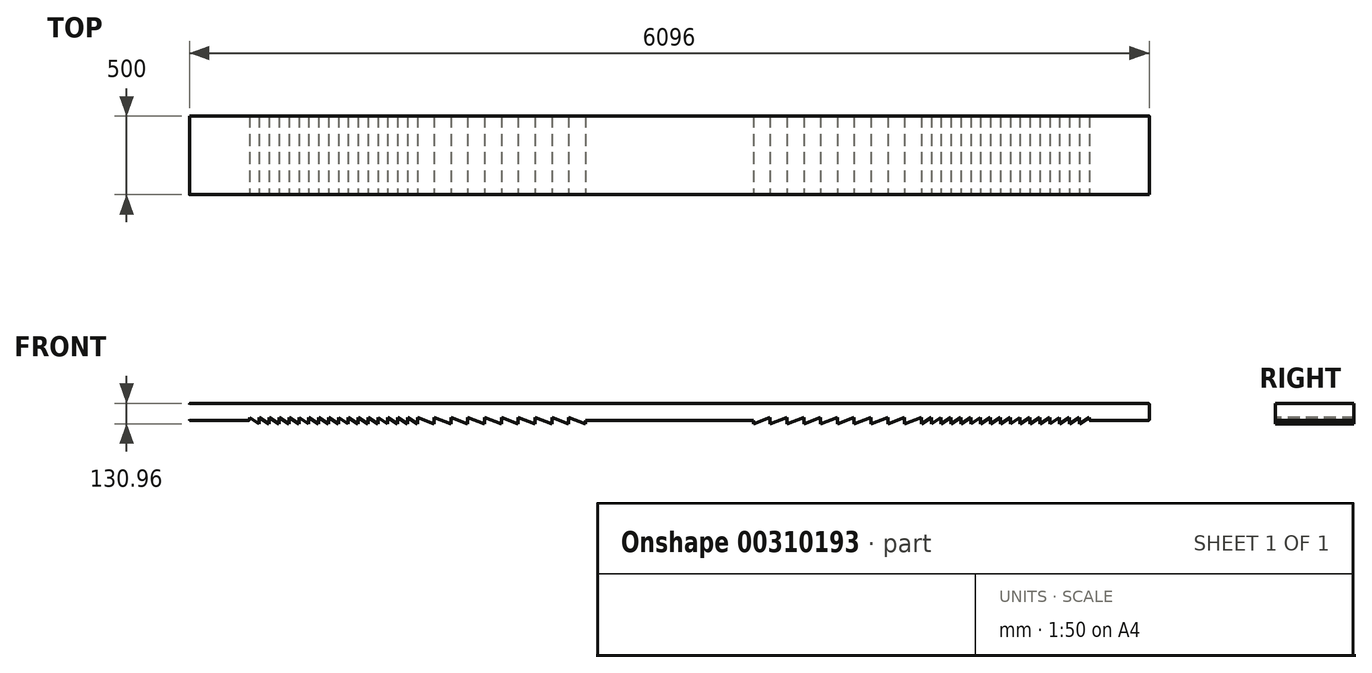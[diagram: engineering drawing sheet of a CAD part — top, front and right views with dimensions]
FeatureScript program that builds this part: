
annotation { "Feature Type Name" : "Feature", "Feature Type Description" : "" }
export const myFeature = defineFeature(function(context is Context, id is Id, definition is map)
    precondition{}
    {
        {
            var Q0;
            Q0=qCreatedBy(makeId("Front.planeOp"),FACE);
            var sketch = newSketch(context, id + "F0", { "sketchPlane" : qUnion([Q0])});
            skLineSegment(sketch, "E0", {"start": v(-3048, 59.13) * mm, "end": v(-3048, -37.9) * mm});
            skArc(sketch, "E1", {"start": v(-3048, -37.9) * mm, "mid": v(-3046.14, -42.4) * mm, "end": v(-3041.65, -44.25) * mm});
            skLineSegment(sketch, "E2", {"start": v(-3041.65, -44.25) * mm, "end": v(-2673.35, -44.25) * mm});
            skArc(sketch, "E3", {"start": v(-2673.35, -44.25) * mm, "mid": v(-2668.86, -42.4) * mm, "end": v(-2667, -37.9) * mm});
            skLineSegment(sketch, "E4", {"start": v(-2667, -37.9) * mm, "end": v(-2667, -23.42) * mm});
            skLineSegment(sketch, "E5", {"start": v(-2667, -23.42) * mm, "end": v(-2604.26, -65.45) * mm});
            skLineSegment(sketch, "E6", {"start": v(-2604.26, -65.45) * mm, "end": v(-2604.26, -23.41) * mm});
            skLineSegment(sketch, "E7", {"start": v(-2604.26, -23.41) * mm, "end": v(-2541.5, -65.45) * mm});
            skLineSegment(sketch, "E8", {"start": v(-2541.5, -65.45) * mm, "end": v(-2541.5, -23.41) * mm});
            skLineSegment(sketch, "E9", {"start": v(-2541.5, -23.41) * mm, "end": v(-2478.76, -65.45) * mm});
            skLineSegment(sketch, "E10", {"start": v(-2478.76, -65.45) * mm, "end": v(-2478.76, -23.41) * mm});
            skLineSegment(sketch, "E11", {"start": v(-2478.76, -23.41) * mm, "end": v(-2416, -65.45) * mm});
            skLineSegment(sketch, "E12", {"start": v(-2416, -65.45) * mm, "end": v(-2416, -23.41) * mm});
            skLineSegment(sketch, "E13", {"start": v(-2416, -23.41) * mm, "end": v(-2353.25, -65.45) * mm});
            skLineSegment(sketch, "E14", {"start": v(-2353.25, -65.45) * mm, "end": v(-2353.25, -23.41) * mm});
            skLineSegment(sketch, "E15", {"start": v(-2353.25, -23.41) * mm, "end": v(-2290.5, -65.45) * mm});
            skLineSegment(sketch, "E16", {"start": v(-2290.5, -65.45) * mm, "end": v(-2290.5, -23.41) * mm});
            skLineSegment(sketch, "E17", {"start": v(-2290.5, -23.41) * mm, "end": v(-2227.74, -65.45) * mm});
            skLineSegment(sketch, "E18", {"start": v(-2227.74, -65.45) * mm, "end": v(-2227.74, -23.41) * mm});
            skLineSegment(sketch, "E19", {"start": v(-2227.74, -23.41) * mm, "end": v(-2165, -65.45) * mm});
            skLineSegment(sketch, "E20", {"start": v(-2165, -65.45) * mm, "end": v(-2165, -23.41) * mm});
            skLineSegment(sketch, "E21", {"start": v(-2165, -23.41) * mm, "end": v(-2102.24, -65.45) * mm});
            skLineSegment(sketch, "E22", {"start": v(-2102.24, -65.45) * mm, "end": v(-2102.24, -23.41) * mm});
            skLineSegment(sketch, "E23", {"start": v(-2102.24, -23.41) * mm, "end": v(-2039.49, -65.45) * mm});
            skLineSegment(sketch, "E24", {"start": v(-2039.49, -65.45) * mm, "end": v(-2039.49, -23.41) * mm});
            skLineSegment(sketch, "E25", {"start": v(-2039.49, -23.41) * mm, "end": v(-1976.73, -65.45) * mm});
            skLineSegment(sketch, "E26", {"start": v(-1976.73, -65.45) * mm, "end": v(-1976.73, -23.41) * mm});
            skLineSegment(sketch, "E27", {"start": v(-1976.73, -23.41) * mm, "end": v(-1913.98, -65.45) * mm});
            skLineSegment(sketch, "E28", {"start": v(-1913.98, -65.45) * mm, "end": v(-1913.98, -23.41) * mm});
            skLineSegment(sketch, "E29", {"start": v(-1913.98, -23.41) * mm, "end": v(-1851.23, -65.45) * mm});
            skLineSegment(sketch, "E30", {"start": v(-1851.23, -65.45) * mm, "end": v(-1851.23, -23.41) * mm});
            skLineSegment(sketch, "E31", {"start": v(-1851.23, -23.41) * mm, "end": v(-1788.47, -65.45) * mm});
            skLineSegment(sketch, "E32", {"start": v(-1788.47, -65.45) * mm, "end": v(-1788.47, -23.41) * mm});
            skLineSegment(sketch, "E33", {"start": v(-1788.47, -23.41) * mm, "end": v(-1725.72, -65.45) * mm});
            skLineSegment(sketch, "E34", {"start": v(-1725.72, -65.45) * mm, "end": v(-1725.72, -23.41) * mm});
            skLineSegment(sketch, "E35", {"start": v(-1725.72, -23.41) * mm, "end": v(-1662.97, -65.45) * mm});
            skLineSegment(sketch, "E36", {"start": v(-1662.97, -65.45) * mm, "end": v(-1662.97, -23.41) * mm});
            skLineSegment(sketch, "E37", {"start": v(-1662.97, -23.41) * mm, "end": v(-1600.21, -65.45) * mm});
            skLineSegment(sketch, "E38", {"start": v(-1600.21, -65.45) * mm, "end": v(-1600.21, -23.42) * mm});
            skLineSegment(sketch, "E39", {"start": v(-1600.21, -23.42) * mm, "end": v(-1493.53, -65.48) * mm});
            skLineSegment(sketch, "E40", {"start": v(-1493.53, -65.48) * mm, "end": v(-1493.53, -23.42) * mm});
            skLineSegment(sketch, "E41", {"start": v(-1493.53, -23.42) * mm, "end": v(-1386.85, -65.48) * mm});
            skLineSegment(sketch, "E42", {"start": v(-1386.85, -65.48) * mm, "end": v(-1386.85, -23.42) * mm});
            skLineSegment(sketch, "E43", {"start": v(-1386.85, -23.42) * mm, "end": v(-1280.17, -65.48) * mm});
            skLineSegment(sketch, "E44", {"start": v(-1280.17, -65.48) * mm, "end": v(-1280.17, -23.42) * mm});
            skLineSegment(sketch, "E45", {"start": v(-1280.17, -23.42) * mm, "end": v(-1173.5, -65.48) * mm});
            skLineSegment(sketch, "E46", {"start": v(-1173.5, -65.48) * mm, "end": v(-1173.5, -23.42) * mm});
            skLineSegment(sketch, "E47", {"start": v(-1173.5, -23.42) * mm, "end": v(-1066.81, -65.48) * mm});
            skLineSegment(sketch, "E48", {"start": v(-1066.81, -65.48) * mm, "end": v(-1066.81, -23.42) * mm});
            skLineSegment(sketch, "E49", {"start": v(-1066.81, -23.42) * mm, "end": v(-960.13, -65.48) * mm});
            skLineSegment(sketch, "E50", {"start": v(-960.13, -65.48) * mm, "end": v(-960.13, -23.42) * mm});
            skLineSegment(sketch, "E51", {"start": v(-960.13, -23.42) * mm, "end": v(-853.45, -65.48) * mm});
            skLineSegment(sketch, "E52", {"start": v(-853.45, -65.48) * mm, "end": v(-853.45, -23.42) * mm});
            skLineSegment(sketch, "E53", {"start": v(-853.45, -23.42) * mm, "end": v(-746.77, -65.48) * mm});
            skLineSegment(sketch, "E54", {"start": v(-746.77, -65.48) * mm, "end": v(-746.77, -23.42) * mm});
            skLineSegment(sketch, "E55", {"start": v(-746.77, -23.42) * mm, "end": v(-640.1, -65.48) * mm});
            skLineSegment(sketch, "E56", {"start": v(-640.1, -65.48) * mm, "end": v(-640.1, -23.42) * mm});
            skLineSegment(sketch, "E57", {"start": v(-640.1, -23.42) * mm, "end": v(-533.41, -65.48) * mm});
            skLineSegment(sketch, "E58", {"start": v(-533.41, -44.25) * mm, "end": v(-533.41, -65.48) * mm});
            skLineSegment(sketch, "E59", {"start": v(-533.41, -44.25) * mm, "end": v(533.41, -44.25) * mm});
            skLineSegment(sketch, "E60", {"start": v(533.41, -44.25) * mm, "end": v(533.41, -65.48) * mm});
            skLineSegment(sketch, "E61", {"start": v(533.41, -65.48) * mm, "end": v(640.1, -23.42) * mm});
            skLineSegment(sketch, "E62", {"start": v(640.1, -23.42) * mm, "end": v(640.1, -65.48) * mm});
            skLineSegment(sketch, "E63", {"start": v(640.1, -65.48) * mm, "end": v(746.77, -23.42) * mm});
            skLineSegment(sketch, "E64", {"start": v(746.77, -23.42) * mm, "end": v(746.77, -65.48) * mm});
            skLineSegment(sketch, "E65", {"start": v(746.77, -65.48) * mm, "end": v(853.45, -23.42) * mm});
            skLineSegment(sketch, "E66", {"start": v(853.45, -23.42) * mm, "end": v(853.45, -65.48) * mm});
            skLineSegment(sketch, "E67", {"start": v(853.45, -65.48) * mm, "end": v(960.13, -23.42) * mm});
            skLineSegment(sketch, "E68", {"start": v(960.13, -23.42) * mm, "end": v(960.13, -65.48) * mm});
            skLineSegment(sketch, "E69", {"start": v(960.13, -65.48) * mm, "end": v(1066.81, -23.42) * mm});
            skLineSegment(sketch, "E70", {"start": v(1066.81, -23.42) * mm, "end": v(1066.81, -65.48) * mm});
            skLineSegment(sketch, "E71", {"start": v(1066.81, -65.48) * mm, "end": v(1173.5, -23.42) * mm});
            skLineSegment(sketch, "E72", {"start": v(1173.5, -23.42) * mm, "end": v(1173.5, -65.48) * mm});
            skLineSegment(sketch, "E73", {"start": v(1173.5, -65.48) * mm, "end": v(1280.17, -23.42) * mm});
            skLineSegment(sketch, "E74", {"start": v(1280.17, -23.42) * mm, "end": v(1280.17, -65.48) * mm});
            skLineSegment(sketch, "E75", {"start": v(1280.17, -65.48) * mm, "end": v(1386.85, -23.42) * mm});
            skLineSegment(sketch, "E76", {"start": v(1386.85, -23.42) * mm, "end": v(1386.85, -65.48) * mm});
            skLineSegment(sketch, "E77", {"start": v(1386.85, -65.48) * mm, "end": v(1493.53, -23.42) * mm});
            skLineSegment(sketch, "E78", {"start": v(1493.53, -23.42) * mm, "end": v(1493.53, -65.48) * mm});
            skLineSegment(sketch, "E79", {"start": v(1493.53, -65.48) * mm, "end": v(1600.21, -23.42) * mm});
            skLineSegment(sketch, "E80", {"start": v(1600.21, -23.42) * mm, "end": v(1600.21, -65.45) * mm});
            skLineSegment(sketch, "E81", {"start": v(1600.21, -65.45) * mm, "end": v(1662.97, -23.41) * mm});
            skLineSegment(sketch, "E82", {"start": v(1662.97, -23.41) * mm, "end": v(1662.97, -65.45) * mm});
            skLineSegment(sketch, "E83", {"start": v(1662.97, -65.45) * mm, "end": v(1725.72, -23.41) * mm});
            skLineSegment(sketch, "E84", {"start": v(1725.72, -23.41) * mm, "end": v(1725.72, -65.45) * mm});
            skLineSegment(sketch, "E85", {"start": v(1725.72, -65.45) * mm, "end": v(1788.47, -23.41) * mm});
            skLineSegment(sketch, "E86", {"start": v(1788.47, -23.41) * mm, "end": v(1788.47, -65.45) * mm});
            skLineSegment(sketch, "E87", {"start": v(1788.47, -65.45) * mm, "end": v(1851.23, -23.41) * mm});
            skLineSegment(sketch, "E88", {"start": v(1851.23, -23.41) * mm, "end": v(1851.23, -65.45) * mm});
            skLineSegment(sketch, "E89", {"start": v(1851.23, -65.45) * mm, "end": v(1913.98, -23.41) * mm});
            skLineSegment(sketch, "E90", {"start": v(1913.98, -23.41) * mm, "end": v(1913.98, -65.45) * mm});
            skLineSegment(sketch, "E91", {"start": v(1913.98, -65.45) * mm, "end": v(1976.73, -23.41) * mm});
            skLineSegment(sketch, "E92", {"start": v(1976.73, -23.41) * mm, "end": v(1976.73, -65.45) * mm});
            skLineSegment(sketch, "E93", {"start": v(1976.73, -65.45) * mm, "end": v(2039.49, -23.41) * mm});
            skLineSegment(sketch, "E94", {"start": v(2039.49, -23.41) * mm, "end": v(2039.49, -65.45) * mm});
            skLineSegment(sketch, "E95", {"start": v(2039.49, -65.45) * mm, "end": v(2102.24, -23.41) * mm});
            skLineSegment(sketch, "E96", {"start": v(2102.24, -23.41) * mm, "end": v(2102.24, -65.45) * mm});
            skLineSegment(sketch, "E97", {"start": v(2102.24, -65.45) * mm, "end": v(2165, -23.41) * mm});
            skLineSegment(sketch, "E98", {"start": v(2165, -23.41) * mm, "end": v(2165, -65.45) * mm});
            skLineSegment(sketch, "E99", {"start": v(2165, -65.45) * mm, "end": v(2227.74, -23.41) * mm});
            skLineSegment(sketch, "E100", {"start": v(2227.74, -23.41) * mm, "end": v(2227.74, -65.45) * mm});
            skLineSegment(sketch, "E101", {"start": v(2227.74, -65.45) * mm, "end": v(2290.5, -23.41) * mm});
            skLineSegment(sketch, "E102", {"start": v(2290.5, -23.41) * mm, "end": v(2290.5, -65.45) * mm});
            skLineSegment(sketch, "E103", {"start": v(2290.5, -65.45) * mm, "end": v(2353.25, -23.41) * mm});
            skLineSegment(sketch, "E104", {"start": v(2353.25, -23.41) * mm, "end": v(2353.25, -65.45) * mm});
            skLineSegment(sketch, "E105", {"start": v(2353.25, -65.45) * mm, "end": v(2416, -23.41) * mm});
            skLineSegment(sketch, "E106", {"start": v(2416, -23.41) * mm, "end": v(2416, -65.45) * mm});
            skLineSegment(sketch, "E107", {"start": v(2416, -65.45) * mm, "end": v(2478.76, -23.41) * mm});
            skLineSegment(sketch, "E108", {"start": v(2478.76, -23.41) * mm, "end": v(2478.76, -65.45) * mm});
            skLineSegment(sketch, "E109", {"start": v(2478.76, -65.45) * mm, "end": v(2541.5, -23.41) * mm});
            skLineSegment(sketch, "E110", {"start": v(2541.5, -23.41) * mm, "end": v(2541.5, -65.45) * mm});
            skLineSegment(sketch, "E111", {"start": v(2541.5, -65.45) * mm, "end": v(2604.26, -23.41) * mm});
            skLineSegment(sketch, "E112", {"start": v(2604.26, -23.41) * mm, "end": v(2604.26, -65.45) * mm});
            skLineSegment(sketch, "E113", {"start": v(2604.26, -65.45) * mm, "end": v(2667, -23.42) * mm});
            skLineSegment(sketch, "E114", {"start": v(2667, -37.9) * mm, "end": v(2667, -23.42) * mm});
            skArc(sketch, "E115", {"start": v(2667, -37.9) * mm, "mid": v(2668.86, -42.4) * mm, "end": v(2673.35, -44.25) * mm});
            skLineSegment(sketch, "E116", {"start": v(2673.35, -44.25) * mm, "end": v(3041.65, -44.25) * mm});
            skArc(sketch, "E117", {"start": v(3041.65, -44.25) * mm, "mid": v(3046.14, -42.4) * mm, "end": v(3048, -37.9) * mm});
            skLineSegment(sketch, "E118", {"start": v(3048, -37.9) * mm, "end": v(3048, 59.13) * mm});
            skLineSegment(sketch, "E119", {"start": v(3041.65, 65.48) * mm, "end": v(-3041.65, 65.48) * mm});
            skArc(sketch, "E120", {"start": v(-3041.65, 65.48) * mm, "mid": v(-3046.14, 63.62) * mm, "end": v(-3048, 59.13) * mm});
            skArc(sketch, "E121", {"start": v(3048, 59.13) * mm, "mid": v(3046.14, 63.62) * mm, "end": v(3041.65, 65.48) * mm});
            skSolve(sketch);
        }
        {
            var Q0;
            Q0=sQuery(id+"F0.wireOp",EDGE,"E119");
            var Q1;
            Q1=sQuery(id+"F0.wireOp",EDGE,"E2");
            var Q2;
            Q2=sQuery(id+"F0.wireOp",EDGE,"E116");
            var Q3;
            Q3=sQuery(id+"F0.wireOp",EDGE,"E59");
            var Q4;
            Q4=sQuery(id+"F0.wireOp",EDGE,"E50");
            var Q5;
            Q5=sQuery(id+"F0.wireOp",EDGE,"E66");
            var Q6;
            Q6=sQuery(id+"F0.wireOp",EDGE,"E73");
            var Q7;
            Q7=sQuery(id+"F0.wireOp",EDGE,"E105");
            var Q8;
            Q8=sQuery(id+"F0.wireOp",EDGE,"E41");
            var Q9;
            Q9=sQuery(id+"F0.wireOp",EDGE,"E49");
            var Q10;
            Q10=sQuery(id+"F0.wireOp",EDGE,"E65");
            var Q11;
            Q11=sQuery(id+"F0.wireOp",EDGE,"E72");
            var Q12;
            Q12=sQuery(id+"F0.wireOp",EDGE,"E104");
            var Q13;
            Q13=sQuery(id+"F0.wireOp",EDGE,"E40");
            var Q14;
            Q14=sQuery(id+"F0.wireOp",EDGE,"E56");
            var Q15;
            Q15=sQuery(id+"F0.wireOp",EDGE,"E48");
            var Q16;
            Q16=sQuery(id+"F0.wireOp",EDGE,"E64");
            var Q17;
            Q17=sQuery(id+"F0.wireOp",EDGE,"E71");
            var Q18;
            Q18=sQuery(id+"F0.wireOp",EDGE,"E103");
            var Q19;
            Q19=sQuery(id+"F0.wireOp",EDGE,"E55");
            var Q20;
            Q20=sQuery(id+"F0.wireOp",EDGE,"E102");
            var Q21;
            Q21=sQuery(id+"F0.wireOp",EDGE,"E47");
            var Q22;
            Q22=sQuery(id+"F0.wireOp",EDGE,"E54");
            var Q23;
            Q23=sQuery(id+"F0.wireOp",EDGE,"E70");
            var Q24;
            Q24=sQuery(id+"F0.wireOp",EDGE,"E79");
            var Q25;
            Q25=sQuery(id+"F0.wireOp",EDGE,"E101");
            var Q26;
            Q26=sQuery(id+"F0.wireOp",EDGE,"E46");
            var Q27;
            Q27=sQuery(id+"F0.wireOp",EDGE,"E53");
            var Q28;
            Q28=sQuery(id+"F0.wireOp",EDGE,"E69");
            var Q29;
            Q29=sQuery(id+"F0.wireOp",EDGE,"E78");
            var Q30;
            Q30=sQuery(id+"F0.wireOp",EDGE,"E76");
            var Q31;
            Q31=sQuery(id+"F0.wireOp",EDGE,"E44");
            var Q32;
            Q32=sQuery(id+"F0.wireOp",EDGE,"E60");
            var Q33;
            Q33=sQuery(id+"F0.wireOp",EDGE,"E45");
            var Q34;
            Q34=sQuery(id+"F0.wireOp",EDGE,"E52");
            var Q35;
            Q35=sQuery(id+"F0.wireOp",EDGE,"E68");
            var Q36;
            Q36=sQuery(id+"F0.wireOp",EDGE,"E77");
            var Q37;
            Q37=sQuery(id+"F0.wireOp",EDGE,"E75");
            var Q38;
            Q38=sQuery(id+"F0.wireOp",EDGE,"E43");
            var Q39;
            Q39=sQuery(id+"F0.wireOp",EDGE,"E51");
            var Q40;
            Q40=sQuery(id+"F0.wireOp",EDGE,"E67");
            var Q41;
            Q41=sQuery(id+"F0.wireOp",EDGE,"E18");
            var Q42;
            Q42=sQuery(id+"F0.wireOp",EDGE,"E25");
            var Q43;
            Q43=sQuery(id+"F0.wireOp",EDGE,"E87");
            var Q44;
            Q44=sQuery(id+"F0.wireOp",EDGE,"E39");
            var Q45;
            Q45=sQuery(id+"F0.wireOp",EDGE,"E95");
            var Q46;
            Q46=sQuery(id+"F0.wireOp",EDGE,"E111");
            var Q47;
            Q47=sQuery(id+"F0.wireOp",EDGE,"E63");
            var Q48;
            Q48=sQuery(id+"F0.wireOp",EDGE,"E86");
            var Q49;
            Q49=sQuery(id+"F0.wireOp",EDGE,"E94");
            var Q50;
            Q50=sQuery(id+"F0.wireOp",EDGE,"E110");
            var Q51;
            Q51=sQuery(id+"F0.wireOp",EDGE,"E62");
            var Q52;
            Q52=sQuery(id+"F0.wireOp",EDGE,"E85");
            var Q53;
            Q53=sQuery(id+"F0.wireOp",EDGE,"E108");
            var Q54;
            Q54=sQuery(id+"F0.wireOp",EDGE,"E61");
            var Q55;
            Q55=sQuery(id+"F0.wireOp",EDGE,"E107");
            var Q56;
            Q56=sQuery(id+"F0.wireOp",EDGE,"E27");
            var Q57;
            Q57=sQuery(id+"F0.wireOp",EDGE,"E74");
            var Q58;
            Q58=sQuery(id+"F0.wireOp",EDGE,"E106");
            var Q59;
            Q59=sQuery(id+"F0.wireOp",EDGE,"E42");
            var Q60;
            Q60=sQuery(id+"F0.wireOp",EDGE,"E98");
            var Q61;
            Q61=sQuery(id+"F0.wireOp",EDGE,"E34");
            var Q62;
            Q62=sQuery(id+"F0.wireOp",EDGE,"E82");
            var Q63;
            Q63=sQuery(id+"F0.wireOp",EDGE,"E89");
            var Q64;
            Q64=sQuery(id+"F0.wireOp",EDGE,"E57");
            var Q65;
            Q65=sQuery(id+"F0.wireOp",EDGE,"E97");
            var Q66;
            Q66=sQuery(id+"F0.wireOp",EDGE,"E33");
            var Q67;
            Q67=sQuery(id+"F0.wireOp",EDGE,"E81");
            var Q68;
            Q68=sQuery(id+"F0.wireOp",EDGE,"E17");
            var Q69;
            Q69=sQuery(id+"F0.wireOp",EDGE,"E88");
            var Q70;
            Q70=sQuery(id+"F0.wireOp",EDGE,"E24");
            var Q71;
            Q71=sQuery(id+"F0.wireOp",EDGE,"E32");
            var Q72;
            Q72=sQuery(id+"F0.wireOp",EDGE,"E80");
            var Q73;
            Q73=sQuery(id+"F0.wireOp",EDGE,"E16");
            var Q74;
            Q74=sQuery(id+"F0.wireOp",EDGE,"E23");
            var Q75;
            Q75=sQuery(id+"F0.wireOp",EDGE,"E96");
            var Q76;
            Q76=sQuery(id+"F0.wireOp",EDGE,"E12");
            var Q77;
            Q77=sQuery(id+"F0.wireOp",EDGE,"E11");
            var Q78;
            Q78=sQuery(id+"F0.wireOp",EDGE,"E10");
            var Q79;
            Q79=sQuery(id+"F0.wireOp",EDGE,"E9");
            var Q80;
            Q80=sQuery(id+"F0.wireOp",EDGE,"E8");
            var Q81;
            Q81=sQuery(id+"F0.wireOp",EDGE,"E7");
            var Q82;
            Q82=sQuery(id+"F0.wireOp",EDGE,"E15");
            var Q83;
            Q83=sQuery(id+"F0.wireOp",EDGE,"E14");
            var Q84;
            Q84=sQuery(id+"F0.wireOp",EDGE,"E13");
            var Q85;
            Q85=sQuery(id+"F0.wireOp",EDGE,"E38");
            var Q86;
            Q86=sQuery(id+"F0.wireOp",EDGE,"E31");
            var Q87;
            Q87=sQuery(id+"F0.wireOp",EDGE,"E22");
            var Q88;
            Q88=sQuery(id+"F0.wireOp",EDGE,"E37");
            var Q89;
            Q89=sQuery(id+"F0.wireOp",EDGE,"E30");
            var Q90;
            Q90=sQuery(id+"F0.wireOp",EDGE,"E21");
            var Q91;
            Q91=sQuery(id+"F0.wireOp",EDGE,"E92");
            var Q92;
            Q92=sQuery(id+"F0.wireOp",EDGE,"E28");
            var Q93;
            Q93=sQuery(id+"F0.wireOp",EDGE,"E100");
            var Q94;
            Q94=sQuery(id+"F0.wireOp",EDGE,"E93");
            var Q95;
            Q95=sQuery(id+"F0.wireOp",EDGE,"E109");
            var Q96;
            Q96=sQuery(id+"F0.wireOp",EDGE,"E36");
            var Q97;
            Q97=sQuery(id+"F0.wireOp",EDGE,"E84");
            var Q98;
            Q98=sQuery(id+"F0.wireOp",EDGE,"E20");
            var Q99;
            Q99=sQuery(id+"F0.wireOp",EDGE,"E91");
            var Q100;
            Q100=sQuery(id+"F0.wireOp",EDGE,"E19");
            var Q101;
            Q101=sQuery(id+"F0.wireOp",EDGE,"E26");
            var Q102;
            Q102=sQuery(id+"F0.wireOp",EDGE,"E58");
            var Q103;
            Q103=sQuery(id+"F0.wireOp",EDGE,"E121");
            var Q104;
            Q104=sQuery(id+"F0.wireOp",EDGE,"E120");
            var Q105;
            Q105=sQuery(id+"F0.wireOp",EDGE,"E1");
            var Q106;
            Q106=sQuery(id+"F0.wireOp",EDGE,"E118");
            var Q107;
            Q107=sQuery(id+"F0.wireOp",EDGE,"E29");
            var Q108;
            Q108=sQuery(id+"F0.wireOp",EDGE,"E99");
            var Q109;
            Q109=sQuery(id+"F0.wireOp",EDGE,"E35");
            var Q110;
            Q110=sQuery(id+"F0.wireOp",EDGE,"E83");
            var Q111;
            Q111=sQuery(id+"F0.wireOp",EDGE,"E90");
            var Q112;
            Q112=sQuery(id+"F0.wireOp",EDGE,"E117");
            var Q113;
            Q113=sQuery(id+"F0.wireOp",EDGE,"E114");
            var Q114;
            Q114=sQuery(id+"F0.wireOp",EDGE,"E113");
            var Q115;
            Q115=sQuery(id+"F0.wireOp",EDGE,"E112");
            var Q116;
            Q116=sQuery(id+"F0.wireOp",EDGE,"E6");
            var Q117;
            Q117=sQuery(id+"F0.wireOp",EDGE,"E5");
            var Q118;
            Q118=sQuery(id+"F0.wireOp",EDGE,"E4");
            var Q119;
            Q119=sQuery(id+"F0.wireOp",EDGE,"E115");
            var Q120;
            Q120=sQuery(id+"F0.wireOp",EDGE,"E3");
            extrude(context, id + "F1", {"bodyType" : ToolBodyType.SURFACE, "surfaceEntities" : qUnion([Q0, Q1, Q2, Q3, Q4, Q5, Q6, Q7, Q8, Q9, Q10, Q11, Q12, Q13, Q14, Q15, Q16, Q17, Q18, Q19, Q20, Q21, Q22, Q23, Q24, Q25, Q26, Q27, Q28, Q29, Q30, Q31, Q32, Q33, Q34, Q35, Q36, Q37, Q38, Q39, Q40, Q41, Q42, Q43, Q44, Q45, Q46, Q47, Q48, Q49, Q50, Q51, Q52, Q53, Q54, Q55, Q56, Q57, Q58, Q59, Q60, Q61, Q62, Q63, Q64, Q65, Q66, Q67, Q68, Q69, Q70, Q71, Q72, Q73, Q74, Q75, Q76, Q77, Q78, Q79, Q80, Q81, Q82, Q83, Q84, Q85, Q86, Q87, Q88, Q89, Q90, Q91, Q92, Q93, Q94, Q95, Q96, Q97, Q98, Q99, Q100, Q101, Q102, Q103, Q104, Q105, Q106, Q107, Q108, Q109, Q110, Q111, Q112, Q113, Q114, Q115, Q116, Q117, Q118, Q119, Q120]), "depth" : 500 * mm});
        }
    });
